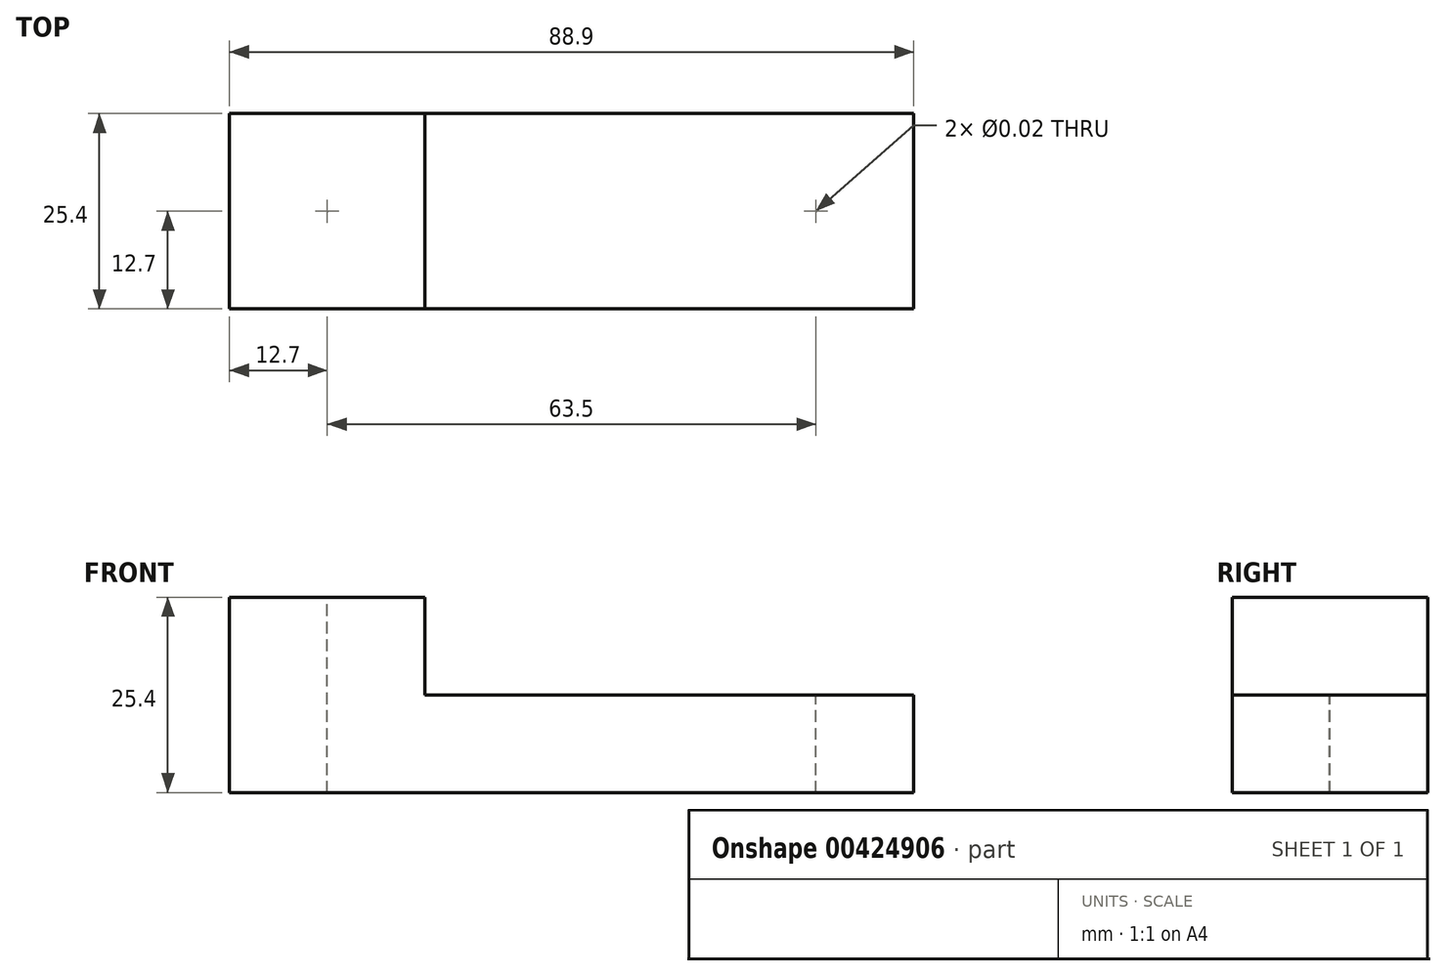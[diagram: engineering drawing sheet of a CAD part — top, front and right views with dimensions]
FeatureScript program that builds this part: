
annotation { "Feature Type Name" : "Feature", "Feature Type Description" : "" }
export const myFeature = defineFeature(function(context is Context, id is Id, definition is map)
    precondition{}
    {
        {
            var Q0;
            Q0=qCreatedBy(makeId("Front.planeOp"),FACE);
            var sketch = newSketch(context, id + "F0", { "sketchPlane" : qUnion([Q0])});
            skLineSegment(sketch, "E0", {"start": v(0, 0) * mm, "end": v(0, -12.7) * mm});
            skLineSegment(sketch, "E1", {"start": v(0, -12.7) * mm, "end": v(-88.9, -12.7) * mm});
            skLineSegment(sketch, "E2", {"start": v(-88.9, -12.7) * mm, "end": v(-88.9, 12.7) * mm});
            skLineSegment(sketch, "E3", {"start": v(-88.9, 12.7) * mm, "end": v(-63.5, 12.7) * mm});
            skLineSegment(sketch, "E4", {"start": v(-63.5, 12.7) * mm, "end": v(-63.5, 0) * mm});
            skLineSegment(sketch, "E5", {"start": v(-63.5, 0) * mm, "end": v(0, 0) * mm});
            skSolve(sketch);
        }
        {
            var Q0;
            Q0=makeQuery(id+"F0.imprint","IMPRINT",FACE,{"disambiguationData":[TD([[makeQuery(id+"F0.imprint","IMPRINT",EDGE,{"derivedFrom":sQuery(id+"F0.wireOp",EDGE,"E0")}),-1.0]])]});
            extrude(context, id + "F1", {"entities" : qUnion([Q0]), "depth" : 25.4 * mm, "symmetric" : true});
        }
        {
            var Q0;
            Q0=makeQuery(id+"F1.opExtrude","SWEPT_FACE",FACE,{"disambiguationData":[OSD([sQuery(id+"F0.wireOp",EDGE,"E1")])]});
            var sketch = newSketch(context, id + "F2", { "sketchPlane" : qUnion([Q0])});
            skLineSegment(sketch, "E6", {"start": v(-88.9, 0) * mm, "end": v(0, 0) * mm, "construction": true});
            skPoint(sketch, "E7", {"position": v(-12.7, 0) * mm});
            skPoint(sketch, "E8", {"position": v(-76.2, 0) * mm});
            skSolve(sketch);
        }
        {
            var Q0;
            Q0=sQuery(id+"F2.wireOp",VERTEX,"E8");
            var Q1;
            Q1=sQuery(id+"F2.wireOp",VERTEX,"E7");
            var Q2;
            Q2=makeQuery(id+"F1.opExtrude","SWEPT_BODY",BODY,{"disambiguationData":[OSD([sQuery(id+"F0.wireOp",EDGE,"E0"),sQuery(id+"F0.wireOp",EDGE,"E1"),sQuery(id+"F0.wireOp",EDGE,"E2"),sQuery(id+"F0.wireOp",EDGE,"E3"),sQuery(id+"F0.wireOp",EDGE,"E4"),sQuery(id+"F0.wireOp",EDGE,"E5")])]});
            hole(context, id + "F3", {"style" : HoleStyle.SIMPLE, "endStyle" : HoleEndStyle.THROUGH, "standardTappedOrClearance" : lookupTablePath({ "standard" : "ANSI", "size" : "1/2 (0.5)", "type" : "Drilled" }), "standardBlindInLast" : lookupTablePath({ "standard" : "ANSI", "size" : "1/2", "type" : "Drilled" }), "holeDiameter" : 1 / 50.8 * mm, "isTappedThrough" : true, "tappedDepth" : 10.3 * mm, "tapClearance" : 3, "locations" : qUnion([Q0, Q1]), "scope" : qUnion([Q2]), "startStyle" : HoleStartStyle.SKETCH});
        }
    });
